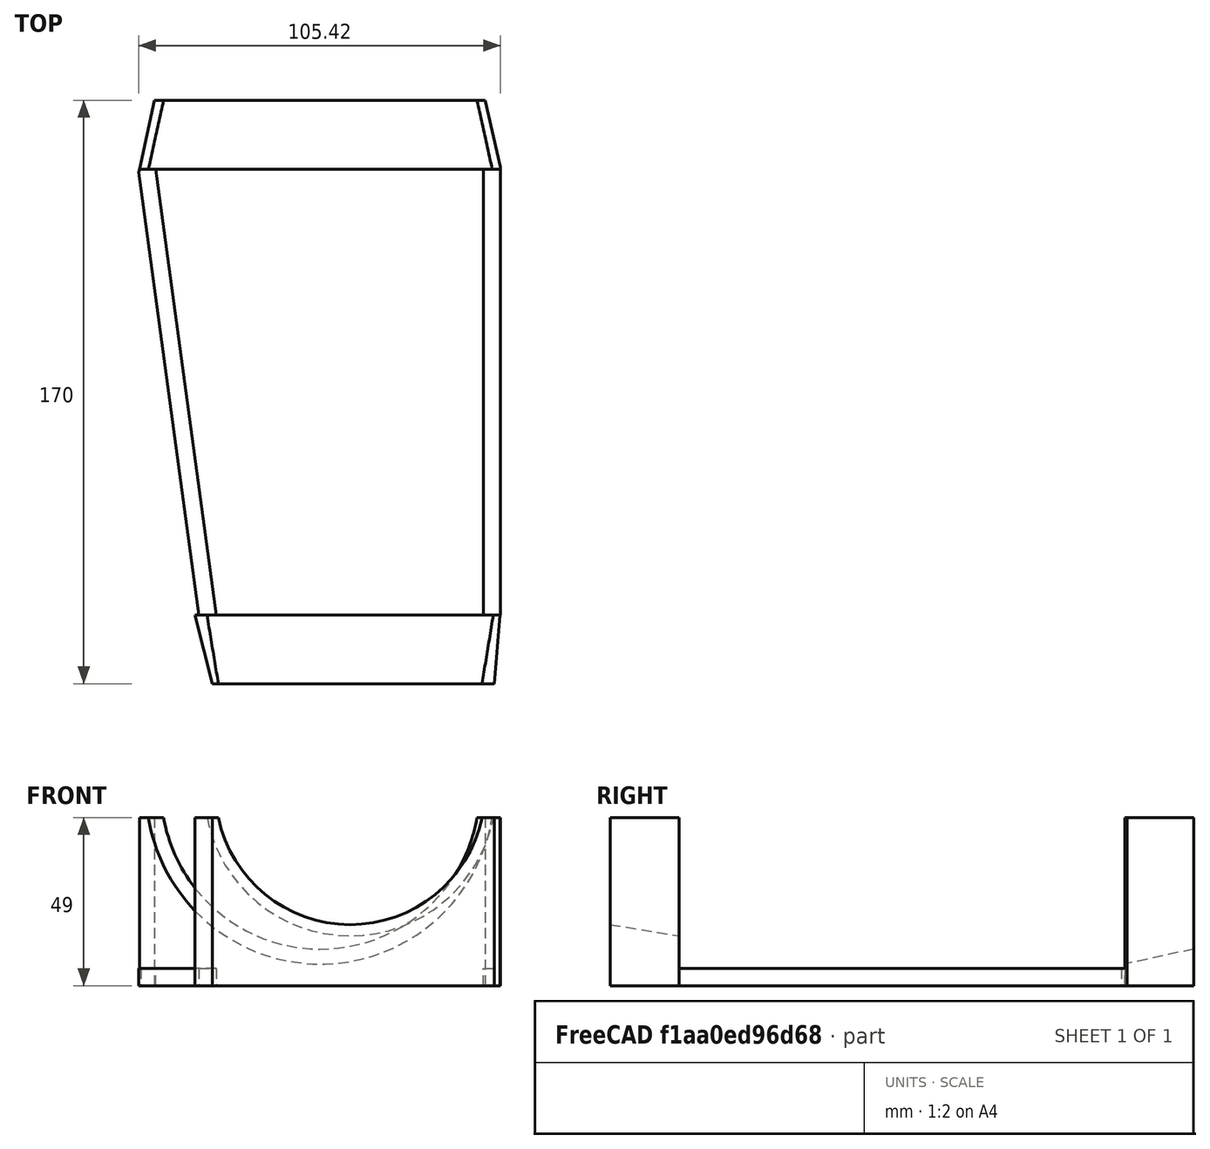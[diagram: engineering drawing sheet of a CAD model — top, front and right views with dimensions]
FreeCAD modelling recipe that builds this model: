
FCSTD DOCUMENT  (FreeCAD 0.19R)
Label: a
License: All rights reserved
LicenseURL: http://en.wikipedia.org/wiki/All_rights_reserved
objects: TechDraw::DrawViewDimension×23, Part::Box×8, Part::Cut×7, Part::Cone×3, TechDraw::DrawProjGroupItem×3, TechDraw::DrawProjGroup×3, Part::MultiFuse×2, TechDraw::DrawSVGTemplate×1, TechDraw::DrawPage×1
note: 20 computed .brp shape members not serialized (recipe doc carries the construction recipe); baked Part::Feature solids carry a one-line shape summary decoded from their .brp

FEATURE [TechDraw::DrawSVGTemplate] Template
  EditableTexts = Designed_by_Name=Designed by Name; Drawing_number=Drawing number; FC-Date=Date; FC-SC=Scale; FC-SH=Sheet; FC-Title=Title; Subtitle=Subtitle; Weight=Weight
  Height = 210
  Orientation = 1
  Width = 297
FEATURE [Part::Box] Box  label="Cube"
  AttacherType = Attacher::AttachEngine3D
  Height = 49
  Length = 89
  Placement = pos=(-123,0,0) rot=(0,0,1;0rad)
  Width = 20
FEATURE [Part::Box] Box001  label="Cube001"
  AttacherType = Attacher::AttachEngine3D
  Height = 49
  Length = 105.5
  Placement = pos=(-139.5,150,0) rot=(0,0,1;0rad)
  Width = 20
FEATURE [Part::Box] Box002  label="Cube002"
  AttacherType = Attacher::AttachEngine3D
  Height = 49
  Length = 40
  Placement = pos=(-143.09,17.91,0) rot=(0,0,-1;1.32645rad)
  Width = 20
FEATURE [Part::Box] Box003  label="Cube003"
  AttacherType = Attacher::AttachEngine3D
  Height = 49
  Length = 40
  Placement = pos=(-38.5947,170.816,0) rot=(0,0,1;4.93579rad)
  Width = 20
FEATURE [Part::Box] Box004  label="Cube004"
  AttacherType = Attacher::AttachEngine3D
  Height = 49
  Length = 40
  Placement = pos=(-152.644,182.723,0) rot=(0,0,1;4.5012rad)
  Width = 20
FEATURE [Part::Box] Box005  label="Cube005"
  AttacherType = Attacher::AttachEngine3D
  Height = 49
  Length = 40
  Placement = pos=(-33.9592,21.5087,0) rot=(0,0,-1;1.65806rad)
  Width = 20
FEATURE [Part::Cut] Cut
  Base = -> Box
  Tool = -> Box005
FEATURE [Part::Cut] Cut001
  Base = -> Cut
  Tool = -> Box002
FEATURE [Part::Cone] Cone
  Angle = 360
  AttacherType = Attacher::AttachEngine3D
  Height = 20.1
  Placement = pos=(-86.5,170,57.03) rot=(-1,0,0;4.71239rad)
  Radius1 = 46.38
  Radius2 = 50.75
FEATURE [Part::Cone] Cone001
  Angle = 360
  AttacherType = Attacher::AttachEngine3D
  Height = 25
  Placement = pos=(-77.7681,22.9763,59.0524) rot=(0.998709,0.043023,-0.027008;1.56127rad)
  Radius1 = 41.5
  Radius2 = 39.25
FEATURE [Part::Cut] Cut002
  Base = -> Cut001
  Tool = -> Cone001
FEATURE [Part::Box] Box007  label="Cube007"
  AttacherType = Attacher::AttachEngine3D
  Height = 5
  Length = 5
  Placement = pos=(-121.333,16.1302,0) rot=(0,0,-1;6.14792rad)
  Width = 135
FEATURE [Part::Box] Box008  label="Cube008"
  AttacherType = Attacher::AttachEngine3D
  Height = 5
  Length = 5
  Placement = pos=(-39,20,0) rot=(0,0,1;0rad)
  Width = 130
FEATURE [Part::Cut] Cut003
  Base = -> Box001
  Tool = -> Box003
FEATURE [Part::MultiFuse] Fusion
  Shapes = -> [Box007,Cut003]
FEATURE [Part::Cone] Cone002
  Angle = 360
  AttacherType = Attacher::AttachEngine3D
  Height = 20.1
  Placement = pos=(-77.8,20.1,57.03) rot=(1,0,0;1.5708rad)
  Radius1 = 42.5
  Radius2 = 39.25
FEATURE [Part::Cut] Cut004
  Base = -> Fusion
  Tool = -> Cone
FEATURE [Part::Cut] Cut005
  Base = -> Cut004
  Tool = -> Box004
FEATURE [Part::Cut] Cut006
  Base = -> Cut002
  Tool = -> Cone002
FEATURE [Part::MultiFuse] Fusion001
  Shapes = -> [Cut006,Cut005,Box008]
FEATURE [TechDraw::DrawProjGroupItem] ProjItem  label="Front"
  CoarseView = false
  Direction = (0,-0.212,0.977)
  Focus = 100
  HardHidden = false
  IsoCount = 0
  IsoHidden = false
  IsoVisible = false
  LockPosition = true
  Perspective = false
  Rotation = 0
  RotationVector = (0.999,-0.002,0)
  ScaleType = 2
  SeamHidden = false
  SeamVisible = true
  SmoothHidden = false
  SmoothVisible = true
  Source = -> [Fusion001]
  Type = 0
  X = 0
  XDirection = (0.00195452,0.97619,0.212258)
  Y = 0
FEATURE [TechDraw::DrawProjGroup] ProjGroup
  Anchor = -> ProjItem
  AutoDistribute = true
  LockPosition = false
  ProjectionType = 0
  Rotation = 0
  ScaleType = 2
  Source = -> [Fusion001]
  Views = -> [ProjItem]
  X = 193.037
  Y = 136.289
  spacingX = 15
  spacingY = 15
FEATURE [TechDraw::DrawViewDimension] Dimension
  Arbitrary = false
  ArbitraryTolerances = false
  EqualTolerance = true
  FormatSpec = %.2f
  FormatSpecOverTolerance = %+.2f
  FormatSpecUnderTolerance = %+.2f
  Inverted = false
  LockPosition = false
  MeasureType = 1
  OverTolerance = 0
  References2D = -> [ProjItem]
  Rotation = 0
  ScaleType = 0
  TheoreticalExact = false
  Type = 0
  UnderTolerance = 0
  X = -1.30053
  Y = -61.1629
FEATURE [TechDraw::DrawViewDimension] Dimension001
  Arbitrary = false
  ArbitraryTolerances = false
  EqualTolerance = true
  FormatSpec = %.2f
  FormatSpecOverTolerance = %+.2f
  FormatSpecUnderTolerance = %+.2f
  Inverted = false
  LockPosition = false
  MeasureType = 1
  OverTolerance = 0
  References2D = -> [ProjItem]
  Rotation = 0
  ScaleType = 0
  TheoreticalExact = false
  Type = 0
  UnderTolerance = 0
  X = 64.0675
  Y = -55.9556
FEATURE [TechDraw::DrawViewDimension] Dimension002
  Arbitrary = false
  ArbitraryTolerances = false
  EqualTolerance = true
  FormatSpec = %.2f
  FormatSpecOverTolerance = %+.2f
  FormatSpecUnderTolerance = %+.2f
  Inverted = false
  LockPosition = false
  MeasureType = 1
  OverTolerance = 0
  References2D = -> [ProjItem]
  Rotation = 0
  ScaleType = 0
  TheoreticalExact = false
  Type = 0
  UnderTolerance = 0
  X = 83.0188
  Y = -61.8967
FEATURE [TechDraw::DrawViewDimension] Dimension003
  Arbitrary = false
  ArbitraryTolerances = false
  EqualTolerance = true
  FormatSpec = %.2f
  FormatSpecOverTolerance = %+.2f
  FormatSpecUnderTolerance = %+.2f
  Inverted = false
  LockPosition = false
  MeasureType = 1
  OverTolerance = 0
  References2D = -> [ProjItem]
  Rotation = 0
  ScaleType = 0
  TheoreticalExact = false
  Type = 0
  UnderTolerance = 0
  X = -0.258889
  Y = 39.5237
FEATURE [TechDraw::DrawViewDimension] Dimension004
  Arbitrary = false
  ArbitraryTolerances = false
  EqualTolerance = true
  FormatSpec = %.2f
  FormatSpecOverTolerance = %+.2f
  FormatSpecUnderTolerance = %+.2f
  Inverted = false
  LockPosition = false
  MeasureType = 1
  OverTolerance = 0
  References2D = -> [ProjItem]
  Rotation = 0
  ScaleType = 0
  TheoreticalExact = false
  Type = 0
  UnderTolerance = 0
  X = 62.9879
  Y = 63.3428
FEATURE [TechDraw::DrawViewDimension] Dimension005
  Arbitrary = false
  ArbitraryTolerances = false
  EqualTolerance = true
  FormatSpec = %.2f
  FormatSpecOverTolerance = %+.2f
  FormatSpecUnderTolerance = %+.2f
  Inverted = false
  LockPosition = false
  MeasureType = 1
  OverTolerance = 0
  References2D = -> [ProjItem]
  Rotation = 0
  ScaleType = 0
  TheoreticalExact = false
  Type = 1
  UnderTolerance = 0
  X = 79.1493
  Y = 63.2005
FEATURE [TechDraw::DrawViewDimension] Dimension006
  Arbitrary = false
  ArbitraryTolerances = false
  EqualTolerance = true
  FormatSpec = %.2f
  FormatSpecOverTolerance = %+.2f
  FormatSpecUnderTolerance = %+.2f
  Inverted = false
  LockPosition = false
  MeasureType = 1
  OverTolerance = 0
  References2D = -> [ProjItem]
  Rotation = 0
  ScaleType = 0
  TheoreticalExact = false
  Type = 0
  UnderTolerance = 0
  X = -70.7892
  Y = 45.5127
FEATURE [TechDraw::DrawViewDimension] Dimension007
  Arbitrary = false
  ArbitraryTolerances = false
  EqualTolerance = true
  FormatSpec = %.2f
  FormatSpecOverTolerance = %+.2f
  FormatSpecUnderTolerance = %+.2f
  Inverted = false
  LockPosition = false
  MeasureType = 1
  OverTolerance = 0
  References2D = -> [ProjItem]
  Rotation = 0
  ScaleType = 0
  TheoreticalExact = false
  Type = 0
  UnderTolerance = 0
  X = -94.2498
  Y = -3.46132
FEATURE [TechDraw::DrawViewDimension] Dimension008
  Arbitrary = false
  ArbitraryTolerances = false
  EqualTolerance = true
  FormatSpec = %.2f
  FormatSpecOverTolerance = %+.2f
  FormatSpecUnderTolerance = %+.2f
  Inverted = false
  LockPosition = false
  MeasureType = 1
  OverTolerance = 0
  References2D = -> [ProjItem]
  Rotation = 0
  ScaleType = 0
  TheoreticalExact = false
  Type = 0
  UnderTolerance = 0
  X = -86.689
  Y = -53.2749
FEATURE [TechDraw::DrawProjGroupItem] ProjItem001  label="Front001"
  CoarseView = false
  Direction = (-0.999117,0.00900894,-0.0410481)
  Focus = 100
  HardHidden = false
  IsoCount = 0
  IsoHidden = false
  IsoVisible = false
  LockPosition = true
  Perspective = false
  Rotation = 0
  RotationVector = (0.999,-0.009,0.041)
  Scale = 0.5
  ScaleType = 2
  SeamHidden = false
  SeamVisible = true
  SmoothHidden = false
  SmoothVisible = true
  Source = -> [Fusion001]
  Type = 0
  X = 0
  XDirection = (-0.041998,-0.178992,0.982954)
  Y = 0
FEATURE [TechDraw::DrawProjGroup] ProjGroup001
  Anchor = -> ProjItem001
  AutoDistribute = true
  LockPosition = false
  ProjectionType = 0
  Rotation = 0
  Scale = 0.5
  ScaleType = 1
  Source = -> [Fusion001]
  Views = -> [ProjItem001]
  X = 52.943
  Y = 140.517
  spacingX = 15
  spacingY = 15
FEATURE [TechDraw::DrawViewDimension] Dimension009
  Arbitrary = false
  ArbitraryTolerances = false
  EqualTolerance = true
  FormatSpec = %.2f
  FormatSpecOverTolerance = %+.2f
  FormatSpecUnderTolerance = %+.2f
  Inverted = false
  LockPosition = false
  MeasureType = 1
  OverTolerance = 0
  References2D = -> [ProjItem001]
  Rotation = 0
  ScaleType = 0
  TheoreticalExact = false
  Type = 0
  UnderTolerance = 0
  X = -13.3676
  Y = 55.624
FEATURE [TechDraw::DrawViewDimension] Dimension010
  Arbitrary = false
  ArbitraryTolerances = false
  EqualTolerance = true
  FormatSpec = %.2f
  FormatSpecOverTolerance = %+.2f
  FormatSpecUnderTolerance = %+.2f
  Inverted = false
  LockPosition = false
  MeasureType = 1
  OverTolerance = 0
  References2D = -> [ProjItem001]
  Rotation = 0
  ScaleType = 0
  TheoreticalExact = false
  Type = 0
  UnderTolerance = 0
  X = 16.8617
  Y = 44.0877
FEATURE [TechDraw::DrawViewDimension] Dimension011
  Arbitrary = false
  ArbitraryTolerances = false
  EqualTolerance = true
  FormatSpec = %.2f
  FormatSpecOverTolerance = %+.2f
  FormatSpecUnderTolerance = %+.2f
  Inverted = false
  LockPosition = false
  MeasureType = 1
  OverTolerance = 0
  References2D = -> [ProjItem001]
  Rotation = 0
  ScaleType = 0
  TheoreticalExact = false
  Type = 0
  UnderTolerance = 0
  X = -24.6972
  Y = 47.5896
FEATURE [TechDraw::DrawViewDimension] Dimension012
  Arbitrary = false
  ArbitraryTolerances = false
  EqualTolerance = true
  FormatSpec = %.2f
  FormatSpecOverTolerance = %+.2f
  FormatSpecUnderTolerance = %+.2f
  Inverted = false
  LockPosition = false
  MeasureType = 1
  OverTolerance = 0
  References2D = -> [ProjItem001]
  Rotation = 0
  ScaleType = 0
  TheoreticalExact = false
  Type = 0
  UnderTolerance = 0
  X = 8.62341
  Y = 8.36907
FEATURE [TechDraw::DrawViewDimension] Dimension013
  Arbitrary = false
  ArbitraryTolerances = false
  EqualTolerance = true
  FormatSpec = %.2f
  FormatSpecOverTolerance = %+.2f
  FormatSpecUnderTolerance = %+.2f
  Inverted = false
  LockPosition = false
  MeasureType = 1
  OverTolerance = 0
  References2D = -> [ProjItem001]
  Rotation = 0
  ScaleType = 0
  TheoreticalExact = false
  Type = 0
  UnderTolerance = 0
  X = -16.4848
  Y = 4.855
FEATURE [TechDraw::DrawViewDimension] Dimension014
  Arbitrary = false
  ArbitraryTolerances = false
  EqualTolerance = true
  FormatSpec = %.2f
  FormatSpecOverTolerance = %+.2f
  FormatSpecUnderTolerance = %+.2f
  Inverted = false
  LockPosition = false
  MeasureType = 1
  OverTolerance = 0
  References2D = -> [ProjItem001]
  Rotation = 0
  ScaleType = 0
  TheoreticalExact = false
  Type = 0
  UnderTolerance = 0
  X = 8.59214
  Y = -44.9726
FEATURE [TechDraw::DrawViewDimension] Dimension015
  Arbitrary = false
  ArbitraryTolerances = false
  EqualTolerance = true
  FormatSpec = %.2f
  FormatSpecOverTolerance = %+.2f
  FormatSpecUnderTolerance = %+.2f
  Inverted = false
  LockPosition = false
  MeasureType = 1
  OverTolerance = 0
  References2D = -> [ProjItem001]
  Rotation = 0
  ScaleType = 0
  TheoreticalExact = false
  Type = 0
  UnderTolerance = 0
  X = 31.0659
  Y = -29.9674
FEATURE [TechDraw::DrawViewDimension] Dimension016
  Arbitrary = false
  ArbitraryTolerances = false
  EqualTolerance = true
  FormatSpec = %.2f
  FormatSpecOverTolerance = %+.2f
  FormatSpecUnderTolerance = %+.2f
  Inverted = false
  LockPosition = false
  MeasureType = 1
  OverTolerance = 0
  References2D = -> [ProjItem001]
  Rotation = 0
  ScaleType = 0
  TheoreticalExact = false
  Type = 0
  UnderTolerance = 0
  X = -6.36977
  Y = -48.6695
FEATURE [TechDraw::DrawProjGroupItem] ProjItem002  label="Front002"
  CoarseView = false
  Direction = (-0.00150811,-0.983809,-0.179212)
  Focus = 100
  HardHidden = false
  IsoCount = 0
  IsoHidden = false
  IsoVisible = false
  LockPosition = true
  Perspective = false
  Rotation = 0
  RotationVector = (0.999,-0.009,0.041)
  Scale = 0.5
  ScaleType = 2
  SeamHidden = false
  SeamVisible = true
  SmoothHidden = false
  SmoothVisible = true
  Source = -> [Fusion001]
  Type = 0
  X = 0
  XDirection = (0.999117,-0.00900894,0.0410481)
  Y = 0
FEATURE [TechDraw::DrawProjGroup] ProjGroup002
  Anchor = -> ProjItem002
  AutoDistribute = true
  LockPosition = false
  ProjectionType = 0
  Rotation = 0
  Scale = 0.5
  ScaleType = 2
  Source = -> [Fusion001]
  Views = -> [ProjItem002]
  X = 64.7819
  Y = 50.5973
  spacingX = 15
  spacingY = 15
FEATURE [TechDraw::DrawViewDimension] Dimension017
  Arbitrary = false
  ArbitraryTolerances = false
  EqualTolerance = true
  FormatSpec = %.2f
  FormatSpecOverTolerance = %+.2f
  FormatSpecUnderTolerance = %+.2f
  Inverted = false
  LockPosition = false
  MeasureType = 1
  OverTolerance = 0
  References2D = -> [ProjItem002]
  Rotation = 0
  ScaleType = 0
  TheoreticalExact = false
  Type = 0
  UnderTolerance = 0
  X = 37.3718
  Y = 8.27602
FEATURE [TechDraw::DrawViewDimension] Dimension018
  Arbitrary = false
  ArbitraryTolerances = false
  EqualTolerance = true
  FormatSpec = %.2f
  FormatSpecOverTolerance = %+.2f
  FormatSpecUnderTolerance = %+.2f
  Inverted = false
  LockPosition = false
  MeasureType = 1
  OverTolerance = 0
  References2D = -> [ProjItem002]
  Rotation = 0
  ScaleType = 0
  TheoreticalExact = false
  Type = 0
  UnderTolerance = 0
  X = 3.09597
  Y = 3.58082
FEATURE [TechDraw::DrawViewDimension] Dimension019
  Arbitrary = false
  ArbitraryTolerances = false
  EqualTolerance = true
  FormatSpec = %.2f
  FormatSpecOverTolerance = %+.2f
  FormatSpecUnderTolerance = %+.2f
  Inverted = false
  LockPosition = false
  MeasureType = 1
  OverTolerance = 0
  References2D = -> [ProjItem002]
  Rotation = 0
  ScaleType = 0
  TheoreticalExact = false
  Type = 0
  UnderTolerance = 0
  X = -0.842503
  Y = -27.2142
FEATURE [TechDraw::DrawViewDimension] Dimension021
  Arbitrary = false
  ArbitraryTolerances = false
  EqualTolerance = true
  FormatSpec = %.2f
  FormatSpecOverTolerance = %+.2f
  FormatSpecUnderTolerance = %+.2f
  Inverted = false
  LockPosition = false
  MeasureType = 1
  OverTolerance = 0
  References2D = -> [ProjItem]
  Rotation = 0
  ScaleType = 0
  TheoreticalExact = false
  Type = 0
  UnderTolerance = 0
  X = 35.5409
  Y = 58.4585
FEATURE [TechDraw::DrawViewDimension] Dimension022
  Arbitrary = false
  ArbitraryTolerances = false
  EqualTolerance = true
  FormatSpec = %.2f
  FormatSpecOverTolerance = %+.2f
  FormatSpecUnderTolerance = %+.2f
  Inverted = false
  LockPosition = false
  MeasureType = 1
  OverTolerance = 0
  References2D = -> [ProjItem002]
  Rotation = 0
  ScaleType = 0
  TheoreticalExact = false
  Type = 0
  UnderTolerance = 0
  X = -36.5888
  Y = -3.89123
FEATURE [TechDraw::DrawViewDimension] Dimension023
  Arbitrary = false
  ArbitraryTolerances = false
  EqualTolerance = true
  FormatSpec = %.2f
  FormatSpecOverTolerance = %+.2f
  FormatSpecUnderTolerance = %+.2f
  Inverted = false
  LockPosition = false
  MeasureType = 1
  OverTolerance = 0
  References2D = -> [ProjItem002]
  Rotation = 0
  ScaleType = 0
  TheoreticalExact = false
  Type = 0
  UnderTolerance = 0
  X = 18.2879
  Y = 28.6699
FEATURE [TechDraw::DrawPage] Page
  KeepUpdated = true
  NextBalloonIndex = 1
  ProjectionType = 0
  Template = -> Template
  Views = -> [ProjGroup,Dimension,Dimension001,Dimension002,Dimension003,Dimension004,Dimension005,Dimension006,Dimension007,Dimension008,ProjGroup001,Dimension009,Dimension010,Dimension011,Dimension012,Dimension013,Dimension014,Dimension015,Dimension016,ProjGroup002,Dimension017,Dimension018,Dimension019,Dimension021,Dimension022,Dimension023]
